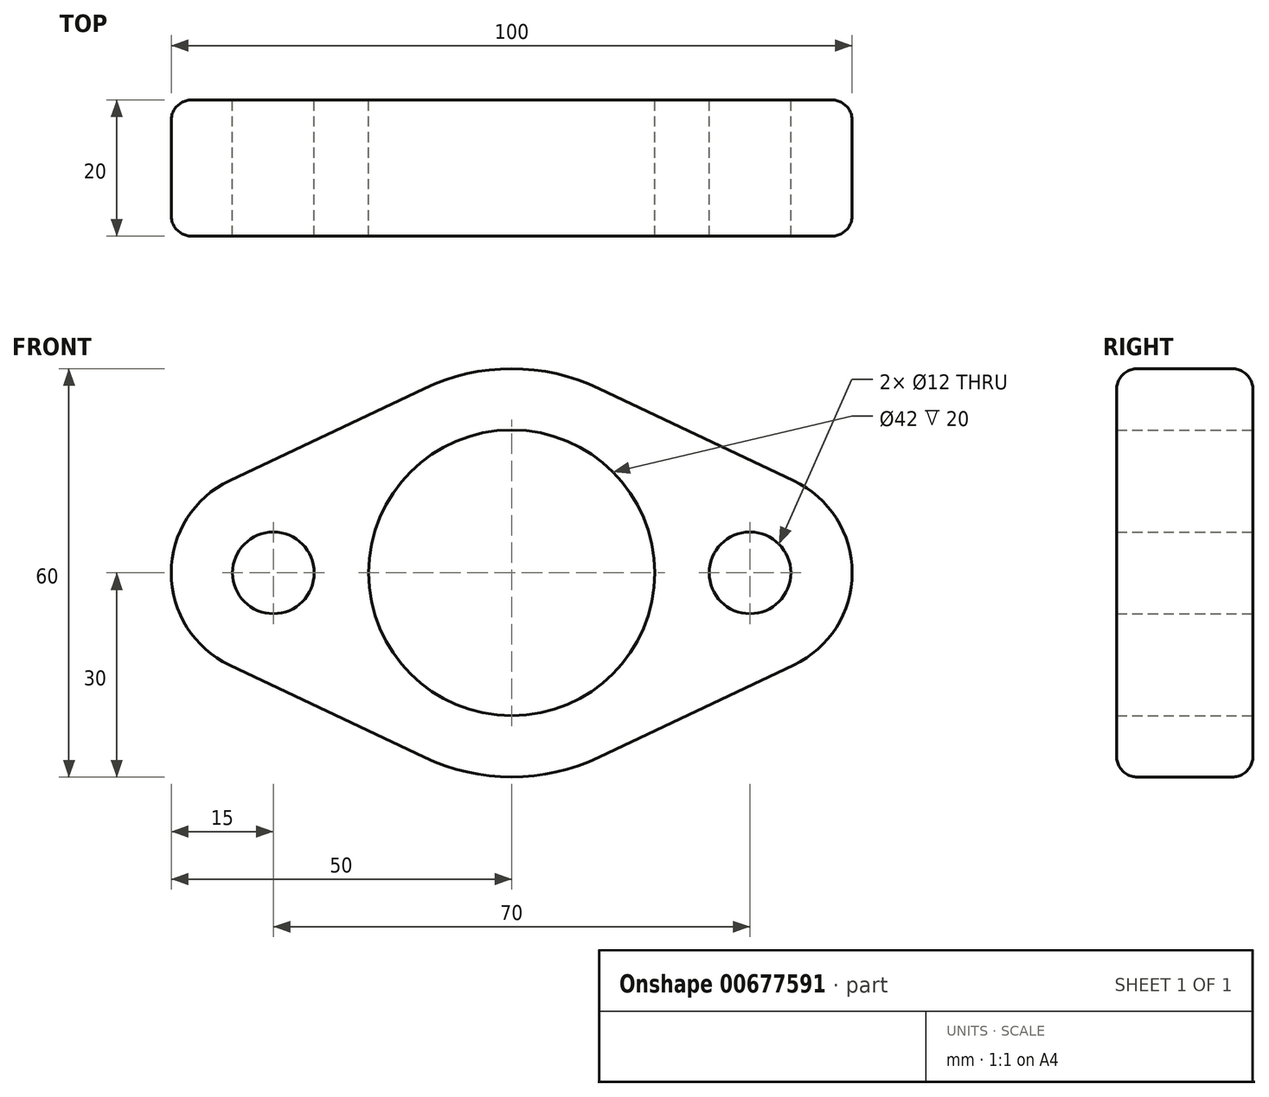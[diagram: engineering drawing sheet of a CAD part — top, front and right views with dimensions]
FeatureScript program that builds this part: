
annotation { "Feature Type Name" : "Feature", "Feature Type Description" : "" }
export const myFeature = defineFeature(function(context is Context, id is Id, definition is map)
    precondition{}
    {
        {
            var Q0;
            Q0=qCreatedBy(makeId("Front.planeOp"),FACE);
            var sketch = newSketch(context, id + "F0", { "sketchPlane" : qUnion([Q0])});
            skArc(sketch, "E0", {"start": v(-12.86, -27.1) * mm, "mid": v(0, -30) * mm, "end": v(12.86, -27.1) * mm});
            skArc(sketch, "E1", {"start": v(-41.43, 13.55) * mm, "mid": v(-50, 0) * mm, "end": v(-41.43, -13.55) * mm});
            skCircle(sketch, "E2", {"center": v(0, 0) * mm, "radius": 21 * mm});
            skArc(sketch, "E3.MirrorC", {"start": v(41.43, 13.55) * mm, "mid": v(50, 0) * mm, "end": v(41.43, -13.55) * mm});
            skCircle(sketch, "E4", {"center": v(-35, 0) * mm, "radius": 6 * mm});
            skCircle(sketch, "E5.MirrorC", {"center": v(35, 0) * mm, "radius": 6 * mm});
            skLineSegment(sketch, "E6", {"start": v(-41.43, 13.55) * mm, "end": v(-12.86, 27.1) * mm});
            skLineSegment(sketch, "E7.MirrorCS", {"start": v(41.43, 13.55) * mm, "end": v(12.86, 27.1) * mm});
            skLineSegment(sketch, "E8.MirrorCS", {"start": v(-41.43, -13.55) * mm, "end": v(-12.86, -27.1) * mm});
            skLineSegment(sketch, "E9.MirrorCS", {"start": v(41.43, -13.55) * mm, "end": v(12.86, -27.1) * mm});
            skArc(sketch, "E10.trimOffspring", {"start": v(12.86, 27.1) * mm, "mid": v(0, 30) * mm, "end": v(-12.86, 27.1) * mm});
            skSolve(sketch);
        }
        {
            var Q0;
            Q0=makeQuery(id+"F0.imprint","IMPRINT",FACE,{"disambiguationData":[TD([[makeQuery(id+"F0.imprint","IMPRINT",EDGE,{"derivedFrom":sQuery(id+"F0.wireOp",EDGE,"E0")}),1.0]])]});
            extrude(context, id + "F1", {"entities" : qUnion([Q0]), "depth" : 10 * mm, "offsetDistance" : 25 * mm, "hasSecondDirection" : true, "secondDirectionOppositeDirection" : true, "secondDirectionDepth" : 10 * mm});
        }
        {
            var Q0;
            Q0=makeQuery(id+"F1.opExtrude","CAP_EDGE",EDGE,{"disambiguationData":[OSD([sQuery(id+"F0.wireOp",EDGE,"E6")])],"isStart":false});
            var Q1;
            Q1=makeQuery(id+"F1.opExtrude","CAP_EDGE",EDGE,{"disambiguationData":[OSD([sQuery(id+"F0.wireOp",EDGE,"E10.trimOffspring")])],"isStart":true});
            fillet(context, id + "F2", {"entities" : qUnion([Q0, Q1]), "radius" : 3 * mm, "tangentPropagation" : true, "allowEdgeOverflow" : false});
        }
    });
